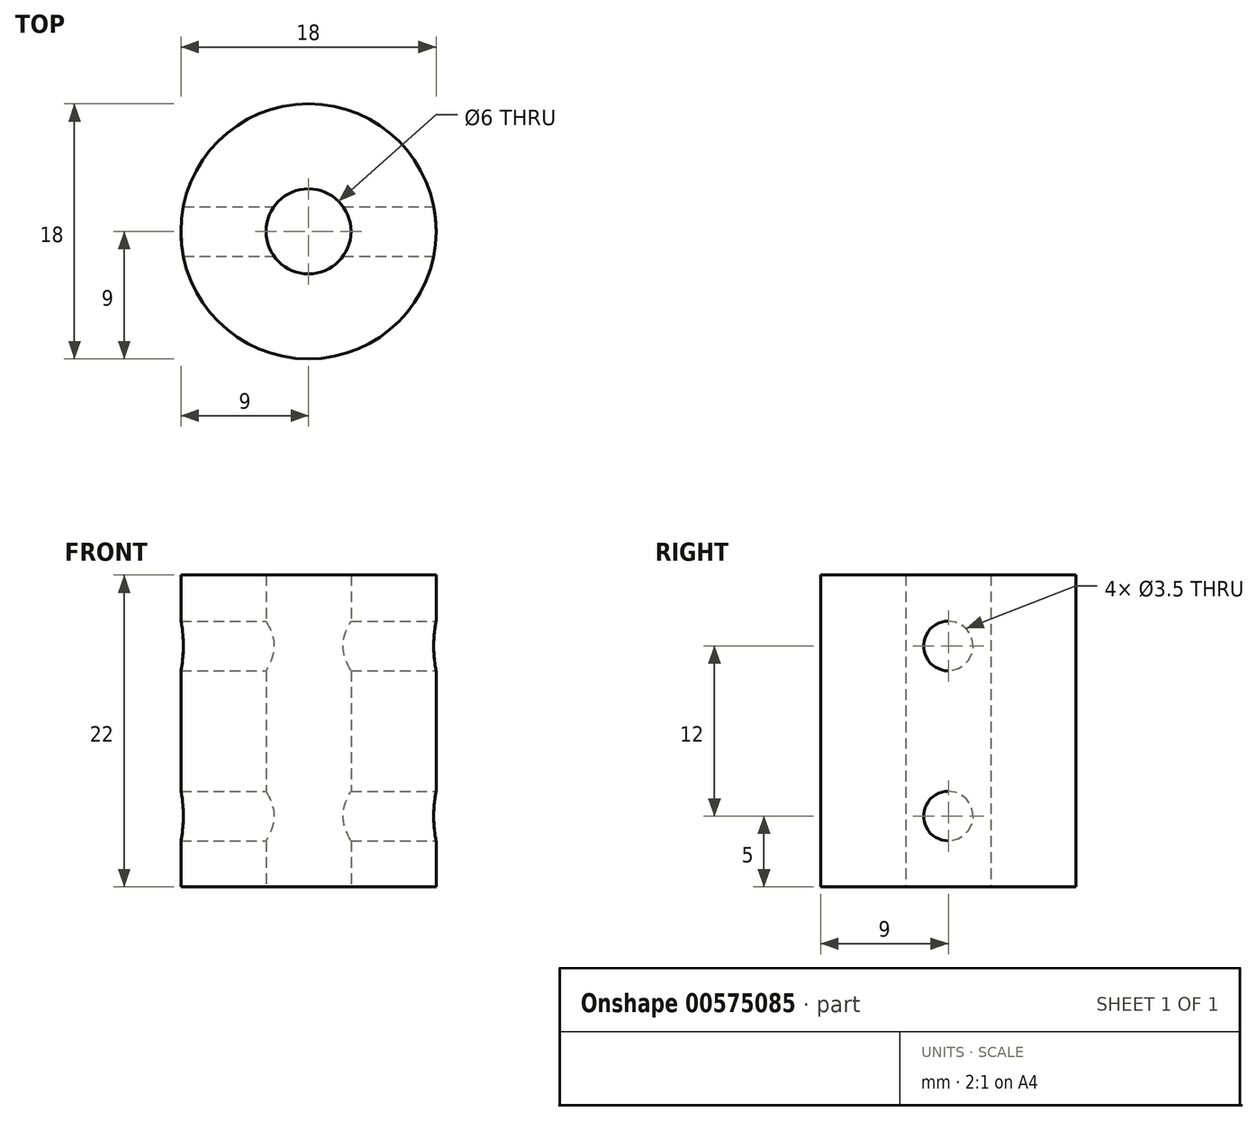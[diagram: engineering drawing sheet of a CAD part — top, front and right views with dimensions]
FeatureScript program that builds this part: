
annotation { "Feature Type Name" : "Feature", "Feature Type Description" : "" }
export const myFeature = defineFeature(function(context is Context, id is Id, definition is map)
    precondition{}
    {
        {
            var Q0;
            Q0=qCreatedBy(makeId("Top.planeOp"),FACE);
            var sketch = newSketch(context, id + "F0", { "sketchPlane" : qUnion([Q0])});
            skCircle(sketch, "E0", {"center": v(0, 0) * mm, "radius": 3 * mm});
            skCircle(sketch, "E1", {"center": v(0, 0) * mm, "radius": 9 * mm});
            skSolve(sketch);
        }
        {
            var Q0;
            Q0=makeQuery(id+"F0.imprint","IMPRINT",FACE,{"disambiguationData":[TD([[makeQuery(id+"F0.imprint","IMPRINT",EDGE,{"derivedFrom":sQuery(id+"F0.wireOp",EDGE,"E0")}),-1.0]])]});
            extrude(context, id + "F1", {"entities" : qUnion([Q0]), "depth" : 22 * mm, "offsetDistance" : 25 * mm});
        }
        {
            var Q0;
            Q0=qCreatedBy(makeId("Right.planeOp"),FACE);
            var sketch = newSketch(context, id + "F2", { "sketchPlane" : qUnion([Q0])});
            skCircle(sketch, "E2", {"center": v(0, 17) * mm, "radius": 1.75 * mm});
            skCircle(sketch, "E3", {"center": v(0, 5) * mm, "radius": 1.75 * mm});
            skCircle(sketch, "E4", {"center": v(0, 5) * mm, "radius": 3 * mm});
            skCircle(sketch, "E5", {"center": v(0, 17) * mm, "radius": 3 * mm});
            skSolve(sketch);
        }
        {
            var Q0;
            Q0=makeQuery(id+"F2.imprint","IMPRINT",FACE,{"disambiguationData":[TD([[makeQuery(id+"F2.imprint","IMPRINT",EDGE,{"derivedFrom":sQuery(id+"F2.wireOp",EDGE,"E3")}),1.0]])]});
            var Q1;
            Q1=makeQuery(id+"F2.imprint","IMPRINT",FACE,{"disambiguationData":[TD([[makeQuery(id+"F2.imprint","IMPRINT",EDGE,{"derivedFrom":sQuery(id+"F2.wireOp",EDGE,"E2")}),1.0]])]});
            extrude(context, id + "F3", {"entities" : qUnion([Q0, Q1]), "operationType" : NewBodyOperationType.REMOVE, "endBound" : BoundingType.THROUGH_ALL, "oppositeDirection" : true, "depth" : 25 * mm, "offsetDistance" : 25 * mm, "hasSecondDirection" : true, "secondDirectionOppositeDirection" : false, "secondDirectionDepth" : 25 * mm});
        }
    });
